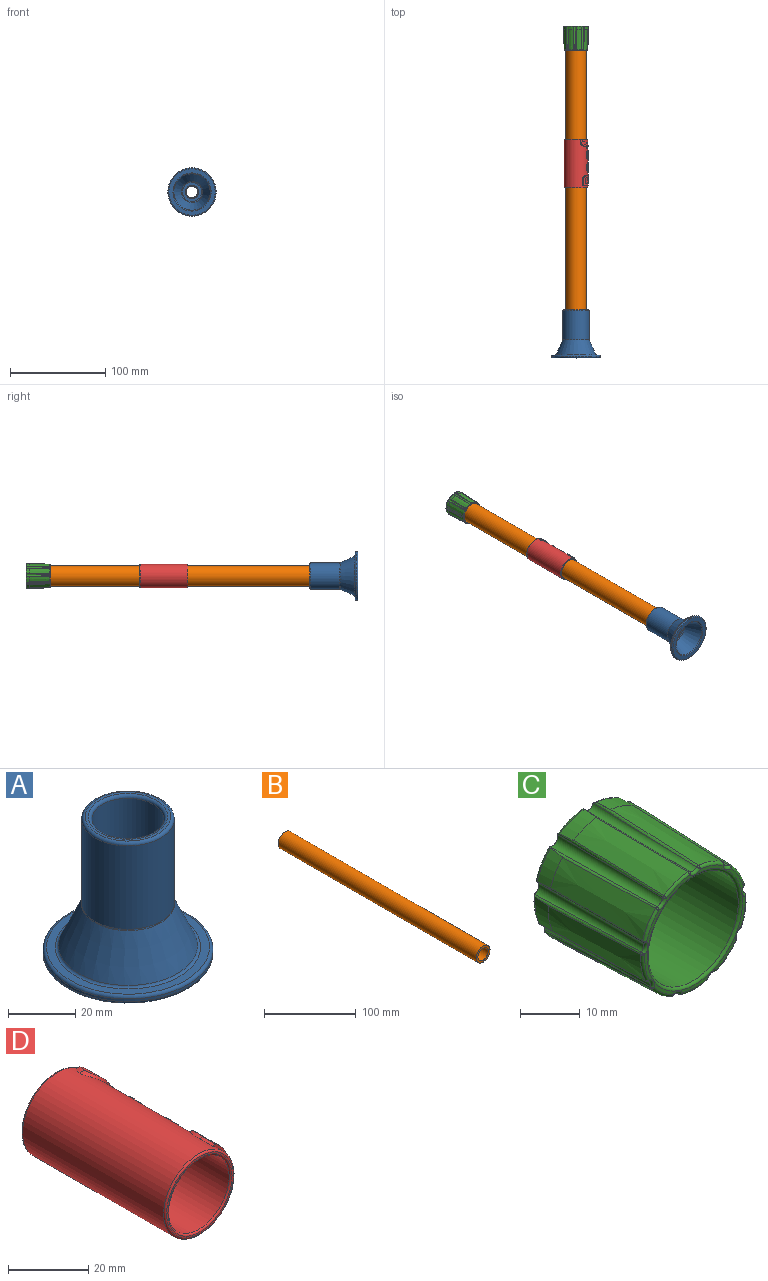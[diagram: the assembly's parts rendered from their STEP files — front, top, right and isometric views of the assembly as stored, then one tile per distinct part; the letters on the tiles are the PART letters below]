
ASSEMBLY  parts=4 mates=3
PART A: 22 faces, bbox 54.9x54.9x50.8 mm
  f0: cylinder r=6mm len=12.01mm, axis (0,0,-1), area 34.8mm2, adj f1,f21
  f1: torus R=7.05mm, axis (0,0,-1), area 66.1mm2, adj f0,f2
  f2: plane 20.23x20.23mm, normal (0,0,-1), area 165.2mm2, adj f1,f3
  f3: torus R=10.12mm, axis (0,0,-1), area 80.8mm2, adj f2,f4
  f4: cone r=19.05mm half-angle=24.1deg, axis (0,0,-1), area 1846.7mm2, adj f3,f5
  f5: torus R=20.01mm, axis (0,0,-1), area 147.6mm2, adj f4,f6
  f6: plane 48.66x48.66mm, normal (0,0,-1), area 602.3mm2, adj f5,f7
  f7: torus R=24.33mm, axis (0,0,-1), area 256.9mm2, adj f6,f8
  f8: cylinder r=25.37mm len=50.75mm, axis (0,0,-1), area 149.8mm2, adj f7,f9
  f9: torus R=24.33mm, axis (0,0,-1), area 256.9mm2, adj f8,f10
  f10: plane 48.66x48.66mm, normal (0,0,1), area 384.5mm2, adj f9,f11
  f11: torus R=21.67mm, axis (0,0,-1), area 159mm2, adj f10,f12
  f12: cone r=13.91mm half-angle=24.1deg, axis (0,0,-1), area 1812.8mm2, adj f11,f13
  f13: torus R=14.87mm, axis (0,0,-1), area 38.5mm2, adj f12,f14
  f14: cylinder r=13.82mm len=30.48mm, axis (0,0,-1), area 2645.9mm2, adj f13,f15
  f15: torus R=12.77mm, axis (0,0,-1), area 139.2mm2, adj f14,f16
  f16: plane 25.54x25.54mm, normal (0,0,1), area 71.4mm2, adj f15,f17
  f17: torus R=11.84mm, axis (0,0,-1), area 115.8mm2, adj f16,f18
  f18: cylinder r=10.79mm len=26.63mm, axis (0,0,-1), area 1806.1mm2, adj f17,f19
  f19: torus R=9.75mm, axis (0,0,-1), area 107.9mm2, adj f18,f20
  f20: plane 19.49x19.49mm, normal (0,0,1), area 142.1mm2, adj f19,f21
  f21: torus R=7.05mm, axis (0,0,-1), area 66.1mm2, adj f0,f20
PART B: 4 faces, bbox 21.3x304.8x21.3 mm
  f0: cylinder r=7.9mm len=304.8mm, axis (0,1,0), area 15128.3mm2, adj f2,f3
  f1: cylinder r=10.67mm len=304.8mm, axis (0,1,0), area 20430.4mm2, adj f2,f3
  f2: plane 21.34x21.34mm, normal (0,-1,0), area 161.5mm2, adj f0,f1
  f3: plane 21.34x21.34mm, normal (0,1,0), area 161.5mm2, adj f0,f1
PART C: 98 faces, bbox 28.5x32.6x28.4 mm
  f0: cylinder r=10.79mm len=21.59mm, axis (0,1,0), area 1271.4mm2, adj f31,f51
  f1: plane 23.87x23.81mm, normal (0,-1,0), area 37.5mm2, adj f41,f42,f43,f44,f45,f46,f47,f48
  f2: cylinder r=13.14mm len=5.84mm, axis (0,1,0), area 18.8mm2, adj f11,f38,f83,f97
  f3: cylinder r=13.14mm len=5.84mm, axis (0,1,0), area 18.8mm2, adj f12,f37,f87,f88
  f4: cylinder r=13.14mm len=5.38mm, axis (0,1,0), area 18.8mm2, adj f13,f36,f67,f92
  f5: cylinder r=13.14mm len=6.12mm, axis (0,1,0), area 18.8mm2, adj f14,f35,f63,f72
  f6: cylinder r=13.14mm len=4.76mm, axis (0,1,0), area 18.8mm2, adj f15,f34,f68,f77
  f7: cylinder r=13.14mm len=6.21mm, axis (0,1,0), area 18.8mm2, adj f16,f33,f73,f82
  f8: cylinder r=13.14mm len=4.76mm, axis (0,1,0), area 18.8mm2, adj f17,f50,f57,f78
  f9: cylinder r=13.14mm len=6.12mm, axis (0,1,0), area 18.8mm2, adj f18,f40,f53,f62
  f10: plane 25.27x25.22mm, normal (0,1,0), area 145.5mm2, adj f21,f22,f23,f24,f25,f26,f27,f28
  f11: cone r=12.43mm half-angle=1.9deg, axis (0,1,0), area 125.3mm2, adj f2,f45,f83,f97
  f12: cone r=12.43mm half-angle=1.9deg, axis (0,1,0), area 125.3mm2, adj f3,f46,f87,f88
  f13: cone r=12.43mm half-angle=1.9deg, axis (0,1,0), area 125.3mm2, adj f4,f47,f67,f92
  f14: cone r=12.43mm half-angle=1.9deg, axis (0,1,0), area 125.3mm2, adj f5,f48,f63,f72
  f15: cone r=12.43mm half-angle=1.9deg, axis (0,1,0), area 125.3mm2, adj f6,f49,f68,f77
  f16: cone r=12.43mm half-angle=1.9deg, axis (0,1,0), area 125.3mm2, adj f7,f41,f73,f82
  f17: cone r=12.43mm half-angle=1.9deg, axis (0,1,0), area 125.3mm2, adj f8,f42,f57,f78
  f18: cone r=12.43mm half-angle=1.9deg, axis (0,1,0), area 125.3mm2, adj f9,f43,f53,f62
  f19: cylinder r=13.14mm len=5.38mm, axis (0,1,0), area 18.8mm2, adj f20,f39,f58,f93
  f20: cone r=12.43mm half-angle=1.9deg, axis (0,1,0), area 125.3mm2, adj f19,f44,f58,f93
  f21: cylinder r=1.27mm len=24.89mm, axis (0,1,0), area 65.3mm2, adj f10,f38,f39,f93,f95,f97
  f22: cylinder r=1.27mm len=24.89mm, axis (0,1,0), area 65.3mm2, adj f10,f39,f40,f58,f60,f62
  f23: cylinder r=1.27mm len=24.89mm, axis (0,1,0), area 65.3mm2, adj f10,f40,f50,f53,f55,f57
  f24: cylinder r=1.27mm len=24.89mm, axis (0,1,0), area 65.3mm2, adj f10,f33,f50,f78,f80,f82
  f25: cylinder r=1.27mm len=24.89mm, axis (0,1,0), area 65.3mm2, adj f10,f33,f34,f73,f75,f77
  f26: cylinder r=1.27mm len=24.89mm, axis (0,1,0), area 65.3mm2, adj f10,f34,f35,f68,f70,f72
  f27: cylinder r=1.27mm len=24.89mm, axis (0,1,0), area 65.3mm2, adj f10,f35,f36,f63,f65,f67
  f28: cylinder r=1.27mm len=24.89mm, axis (0,1,0), area 65.3mm2, adj f10,f36,f37,f88,f90,f92
  f29: cylinder r=1.27mm len=24.89mm, axis (0,1,0), area 65.3mm2, adj f10,f37,f38,f83,f85,f87
  f30: cylinder r=7.94mm len=15.88mm, axis (0,1,0), area 154.5mm2, adj f32,f52
  f31: plane 21.59x21.59mm, normal (0,-1,0), area 142mm2, adj f0,f32
  f32: torus R=8.45mm, axis (0,1,0), area 40.7mm2, adj f30,f31
  f33: torus R=12.64mm, axis (0,-1,0), area 5.1mm2, adj f7,f10,f24,f25,f73,f82
  f34: torus R=12.64mm, axis (0,-1,0), area 5.1mm2, adj f6,f10,f25,f26,f68,f77
  f35: torus R=12.64mm, axis (0,-1,0), area 5.1mm2, adj f5,f10,f26,f27,f63,f72
  f36: torus R=12.64mm, axis (0,-1,0), area 5.1mm2, adj f4,f10,f27,f28,f67,f92
  f37: torus R=12.64mm, axis (0,-1,0), area 5.1mm2, adj f3,f10,f28,f29,f87,f88
  f38: torus R=12.64mm, axis (0,-1,0), area 5.1mm2, adj f2,f10,f21,f29,f83,f97
  f39: torus R=12.64mm, axis (0,-1,0), area 5.1mm2, adj f10,f19,f21,f22,f58,f93
  f40: torus R=12.64mm, axis (0,-1,0), area 5.1mm2, adj f9,f10,f22,f23,f53,f62
  f41: torus R=11.94mm, axis (0,-1,0), area 4.7mm2, adj f1,f16,f74,f81
  f42: torus R=11.94mm, axis (0,-1,0), area 4.7mm2, adj f1,f17,f56,f79
  f43: torus R=11.94mm, axis (0,-1,0), area 4.7mm2, adj f1,f18,f54,f61
  f44: torus R=11.94mm, axis (0,-1,0), area 4.7mm2, adj f1,f20,f59,f94
  f45: torus R=11.94mm, axis (0,-1,0), area 4.7mm2, adj f1,f11,f84,f96
  f46: torus R=11.94mm, axis (0,-1,0), area 4.7mm2, adj f1,f12,f86,f89
  f47: torus R=11.94mm, axis (0,-1,0), area 4.7mm2, adj f1,f13,f66,f91
  f48: torus R=11.94mm, axis (0,-1,0), area 4.7mm2, adj f1,f14,f64,f71
  f49: torus R=11.94mm, axis (0,-1,0), area 4.7mm2, adj f1,f15,f69,f76
  f50: torus R=12.64mm, axis (0,-1,0), area 5.1mm2, adj f8,f10,f23,f24,f57,f78
  f51: torus R=11.3mm, axis (0,-1,0), area 55mm2, adj f0,f1
  f52: torus R=10.48mm, axis (0,-1,0), area 222.1mm2, adj f10,f30
  f53: bspline ~32.55x1.47mm, area 13.9mm2, adj f9,f18,f23,f40,f54
  f54: sphere r=0.51mm, area 0.3mm2, adj f43,f53,f55
  f55: torus R=1.78mm, axis (0,-1,0), area 1.8mm2, adj f1,f23,f54,f56
  f56: sphere r=0.51mm, area 0.3mm2, adj f42,f55,f57
  f57: bspline ~32.59x1.44mm, area 13.9mm2, adj f8,f17,f23,f50,f56
  f58: bspline ~32.55x1.2mm, area 13.9mm2, adj f19,f20,f22,f39,f59
  f59: sphere r=0.51mm, area 0.3mm2, adj f44,f58,f60
  f60: torus R=1.78mm, axis (0,-1,0), area 1.8mm2, adj f1,f22,f59,f61
  f61: sphere r=0.51mm, area 0.3mm2, adj f43,f60,f62
  f62: bspline ~32.51x1.26mm, area 13.9mm2, adj f9,f18,f22,f40,f61
  f63: bspline ~32.51x1.26mm, area 13.9mm2, adj f5,f14,f27,f35,f64
  f64: sphere r=0.51mm, area 0.3mm2, adj f48,f63,f65
  f65: torus R=1.78mm, axis (0,-1,0), area 1.8mm2, adj f1,f27,f64,f66
  f66: sphere r=0.51mm, area 0.3mm2, adj f47,f65,f67
  f67: bspline ~32.56x1.2mm, area 13.9mm2, adj f4,f13,f27,f36,f66
  f68: bspline ~32.59x1.44mm, area 13.9mm2, adj f6,f15,f26,f34,f69
  f69: sphere r=0.51mm, area 0.3mm2, adj f49,f68,f70
  f70: torus R=1.78mm, axis (0,-1,0), area 1.8mm2, adj f1,f26,f69,f71
  f71: sphere r=0.51mm, area 0.3mm2, adj f48,f70,f72
  f72: bspline ~32.55x1.47mm, area 13.9mm2, adj f5,f14,f26,f35,f71
  f73: bspline ~32.52x1.39mm, area 13.9mm2, adj f7,f16,f25,f33,f74
  f74: sphere r=0.51mm, area 0.3mm2, adj f41,f73,f75
  f75: torus R=1.78mm, axis (0,-1,0), area 1.8mm2, adj f1,f25,f74,f76
  f76: sphere r=0.51mm, area 0.3mm2, adj f49,f75,f77
  f77: bspline ~32.58x1.34mm, area 13.9mm2, adj f6,f15,f25,f34,f76
  f78: bspline ~32.58x1.34mm, area 13.9mm2, adj f8,f17,f24,f50,f79
  f79: sphere r=0.51mm, area 0.3mm2, adj f42,f78,f80
  f80: torus R=1.78mm, axis (0,-1,0), area 1.8mm2, adj f1,f24,f79,f81
  f81: sphere r=0.51mm, area 0.3mm2, adj f41,f80,f82
  f82: bspline ~32.52x1.39mm, area 13.9mm2, adj f7,f16,f24,f33,f81
  f83: bspline ~32.53x1.16mm, area 13.9mm2, adj f2,f11,f29,f38,f84
  f84: sphere r=0.51mm, area 0.3mm2, adj f45,f83,f85
  f85: torus R=1.78mm, axis (0,-1,0), area 1.8mm2, adj f1,f29,f84,f86
  f86: sphere r=0.51mm, area 0.3mm2, adj f46,f85,f87
  f87: bspline ~32.53x1.16mm, area 13.9mm2, adj f3,f12,f29,f37,f86
  f88: bspline ~32.57x1.51mm, area 13.9mm2, adj f3,f12,f28,f37,f89
  f89: sphere r=0.51mm, area 0.3mm2, adj f46,f88,f90
  f90: torus R=1.78mm, axis (0,-1,0), area 1.8mm2, adj f1,f28,f89,f91
  f91: sphere r=0.51mm, area 0.3mm2, adj f47,f90,f92
  f92: bspline ~32.59x1.5mm, area 13.9mm2, adj f4,f13,f28,f36,f91
  f93: bspline ~32.58x1.5mm, area 13.9mm2, adj f19,f20,f21,f39,f94
  f94: sphere r=0.51mm, area 0.3mm2, adj f44,f93,f95
  f95: torus R=1.78mm, axis (0,-1,0), area 1.8mm2, adj f1,f21,f94,f96
  f96: sphere r=0.51mm, area 0.3mm2, adj f45,f95,f97
  f97: bspline ~32.57x1.51mm, area 13.9mm2, adj f2,f11,f21,f38,f96
PART D: 96 faces, bbox 26.7x50.8x26.7 mm
  f0: plane 0.8x0.11mm, normal (0,1,0), area 0.1mm2, adj f14,f20,f21,f62
  f1: plane 16.3x6.31mm, normal (0,-1,0), area 13.8mm2, adj f14,f24,f25,f62
  f2: plane 1.17x0.79mm, normal (0,1,0), area 0.9mm2, adj f14,f30,f31,f61
  f3: plane 1.65x1.46mm, normal (0,1,0), area 1.3mm2, adj f14,f34,f35,f61
  f4: plane 1.17x0.79mm, normal (0,1,0), area 0.9mm2, adj f14,f42,f43,f60
  f5: plane 1.65x1.46mm, normal (0,1,0), area 1.3mm2, adj f14,f46,f47,f60
  f6: plane 10.78x2.33mm, normal (0,1,0), area 8.4mm2, adj f14,f50,f58,f59
  f7: plane 10.78x2.33mm, normal (0,-1,0), area 8.4mm2, adj f14,f50,f51,f59
  f8: plane 1.2x0.84mm, normal (0,-1,0), area 0.7mm2, adj f9,f14,f51,f59
  f9: plane 2.2x1.23mm, normal (0,-0.29,0.96), area 2mm2, adj f8,f10,f14,f59
  f10: plane 1.3x0.68mm, normal (0,-1,0), area 0.6mm2, adj f9,f14,f52,f59
  f11: plane 3.54x1.53mm, normal (0,0.95,-0.31), area 2.1mm2, adj f14,f53,f54,f59
  f12: plane 1.37x0.79mm, normal (0,1,0), area 0.7mm2, adj f14,f56,f57,f59
  f13: plane 1.53x1.44mm, normal (0,1,0), area 1.2mm2, adj f14,f57,f58,f59
  f14: cylinder r=12.31mm len=49.78mm, axis (0,1,0), area 3445mm2, adj f0,f1,f2,f3,f4,f5,f6,f7
  f15: plane 23.6x23.6mm, normal (0,-1,0), area 35.9mm2, adj f94,f95
  f16: plane 23.6x23.6mm, normal (0,1,0), area 35.9mm2, adj f92,f93
  f17: extruded ~4.69x2.4mm, area 6mm2, adj f14,f18,f25,f62
  f18: extruded ~3.43x3.07mm, area 3.5mm2, adj f14,f17,f19,f62
  f19: extruded ~2.39x1.88mm, area 2.1mm2, adj f14,f18,f20,f62
  f20: extruded ~2.36x1.22mm, area 2.1mm2, adj f0,f14,f19,f62
  f21: extruded ~3.9x3.71mm, area 4.5mm2, adj f0,f14,f22,f62
  f22: extruded ~3.41x1.65mm, area 3mm2, adj f14,f21,f23,f62
  f23: extruded ~4.13x1.42mm, area 3.7mm2, adj f14,f22,f24,f62
  f24: plane 5.69x0.86mm, normal (0,0,-1), area 4.9mm2, adj f1,f14,f23,f62
  f25: plane 4.61x1.3mm, normal (0,0,1), area 6mm2, adj f1,f14,f17,f62
  f26: extruded ~4.58x1.64mm, area 3.8mm2, adj f14,f27,f37,f61
  f27: extruded ~4.7x1.68mm, area 3.9mm2, adj f14,f26,f28,f61
  f28: extruded ~3.91x1.74mm, area 3.8mm2, adj f14,f27,f29,f61
  f29: extruded ~3.63x1.61mm, area 3.5mm2, adj f14,f28,f30,f61
  f30: extruded ~3.99x1.75mm, area 3.4mm2, adj f2,f14,f29,f61
  f31: plane 8.42x0.76mm, normal (0,0,-1), area 6.4mm2, adj f2,f14,f32,f61
  f32: extruded ~3.27x1.26mm, area 2.7mm2, adj f14,f31,f33,f61
  f33: extruded ~2.9x1.18mm, area 2.6mm2, adj f14,f32,f34,f61
  f34: extruded ~3.9x1.09mm, area 3.2mm2, adj f3,f14,f33,f61
  f35: extruded ~1.86x1.16mm, area 1.7mm2, adj f3,f14,f36,f61
  f36: extruded ~2.11x0.97mm, area 1.8mm2, adj f14,f35,f37,f61
  f37: extruded ~4.28x1.65mm, area 4mm2, adj f14,f26,f36,f61
  f38: extruded ~4.58x1.64mm, area 3.8mm2, adj f14,f39,f49,f60
  f39: extruded ~4.7x1.68mm, area 3.9mm2, adj f14,f38,f40,f60
  f40: extruded ~3.91x1.74mm, area 3.8mm2, adj f14,f39,f41,f60
  f41: extruded ~3.63x1.61mm, area 3.5mm2, adj f14,f40,f42,f60
  f42: extruded ~3.99x1.75mm, area 3.4mm2, adj f4,f14,f41,f60
  f43: plane 8.42x0.76mm, normal (0,0,-1), area 6.4mm2, adj f4,f14,f44,f60
  f44: extruded ~3.27x1.26mm, area 2.7mm2, adj f14,f43,f45,f60
  f45: extruded ~2.9x1.18mm, area 2.6mm2, adj f14,f44,f46,f60
  f46: extruded ~3.9x1.09mm, area 3.2mm2, adj f5,f14,f45,f60
  f47: extruded ~1.86x1.16mm, area 1.7mm2, adj f5,f14,f48,f60
  f48: extruded ~2.11x0.97mm, area 1.8mm2, adj f14,f47,f49,f60
  f49: extruded ~4.28x1.65mm, area 4mm2, adj f14,f38,f48,f60
  f50: plane 1.85x0.86mm, normal (0,0,-1), area 1.6mm2, adj f6,f7,f14,f59
  f51: plane 2.18x0.82mm, normal (0,0,-1), area 1.8mm2, adj f7,f8,f14,f59
  f52: extruded ~6.57x4.51mm, area 9mm2, adj f10,f14,f53,f59
  f53: extruded ~2.44x2.28mm, area 3.9mm2, adj f11,f14,f52,f59
  f54: extruded ~1.83x1.61mm, area 2.2mm2, adj f11,f14,f55,f59
  f55: extruded ~1.97x1.55mm, area 2.1mm2, adj f14,f54,f56,f59
  f56: extruded ~2.89x2.24mm, area 2.3mm2, adj f12,f14,f55,f59
  f57: plane 3.11x0.87mm, normal (0,0,1), area 2.7mm2, adj f12,f13,f14,f59
  f58: plane 3.11x0.82mm, normal (0,0,-1), area 2.5mm2, adj f6,f13,f14,f59
  f59: cylinder r=13.06mm len=17.47mm, axis (0,1,0), area 52.5mm2, adj f6,f7,f8,f9,f10,f11,f12,f13
  f60: cylinder r=13.06mm len=12.67mm, axis (0,1,0), area 62.3mm2, adj f4,f5,f38,f39,f40,f41,f42,f43
  f61: cylinder r=13.06mm len=12.67mm, axis (0,1,0), area 62.3mm2, adj f2,f3,f26,f27,f28,f29,f30,f31
  f62: cylinder r=13.06mm len=16.3mm, axis (0,1,0), area 102.4mm2, adj f0,f1,f17,f18,f19,f20,f21,f22
  f63: cylinder r=12.31mm len=6.89mm, axis (0,1,0), area 39.2mm2, adj f64,f65,f66,f67,f68,f69,f70
  f64: plane 3.12x0.78mm, normal (0,0,1), area 2.4mm2, adj f62,f63,f65,f70
  f65: plane 5.34x3.88mm, normal (0,1,0), area 4.7mm2, adj f62,f63,f64,f66
  f66: plane 2.79x1.03mm, normal (0,0,-1), area 2.9mm2, adj f62,f63,f65,f67
  f67: extruded ~3.12x1.54mm, area 3.3mm2, adj f62,f63,f66,f68
  f68: extruded ~2.25x1.98mm, area 2.1mm2, adj f62,f63,f67,f69
  f69: extruded ~2.12x1.74mm, area 2mm2, adj f62,f63,f68,f70
  f70: extruded ~2.89x0.98mm, area 2.4mm2, adj f62,f63,f64,f69
  f71: cylinder r=12.31mm len=6.39mm, axis (0,1,0), area 19.2mm2, adj f72,f73,f74,f75,f76
  f72: extruded ~2.35x1.16mm, area 2.1mm2, adj f60,f71,f73,f76
  f73: extruded ~2.23x1.15mm, area 2mm2, adj f60,f71,f72,f74
  f74: extruded ~2.68x1.34mm, area 2.2mm2, adj f60,f71,f73,f75
  f75: plane 6.39x0.76mm, normal (0,0,1), area 4.9mm2, adj f60,f71,f74,f76
  f76: extruded ~2.65x1.34mm, area 2.2mm2, adj f60,f71,f72,f75
  f77: cylinder r=12.31mm len=6.39mm, axis (0,1,0), area 19.2mm2, adj f78,f79,f80,f81,f82
  f78: extruded ~2.35x1.16mm, area 2.1mm2, adj f61,f77,f79,f82
  f79: extruded ~2.23x1.15mm, area 2mm2, adj f61,f77,f78,f80
  f80: extruded ~2.68x1.34mm, area 2.2mm2, adj f61,f77,f79,f81
  f81: plane 6.39x0.76mm, normal (0,0,1), area 4.9mm2, adj f61,f77,f80,f82
  f82: extruded ~2.65x1.34mm, area 2.2mm2, adj f61,f77,f78,f81
  f83: cylinder r=12.31mm len=7.37mm, axis (0,1,0), area 41.6mm2, adj f84,f85,f86,f87,f88,f89,f90
  f84: plane 6.1x1.57mm, normal (0,1,0), area 4.7mm2, adj f62,f83,f85,f90
  f85: plane 3.25x0.76mm, normal (0,0,-1), area 2.5mm2, adj f62,f83,f84,f86
  f86: extruded ~3.1x0.84mm, area 2.5mm2, adj f62,f83,f85,f87
  f87: extruded ~2.23x1.02mm, area 1.9mm2, adj f62,f83,f86,f88
  f88: extruded ~2.39x1.25mm, area 2.1mm2, adj f62,f83,f87,f89
  f89: extruded ~2.97x1.05mm, area 2.5mm2, adj f62,f83,f88,f90
  f90: plane 3.4x0.81mm, normal (0,0,1), area 2.7mm2, adj f62,f83,f84,f89
  f91: cylinder r=10.79mm len=49.78mm, axis (0,1,0), area 3376.7mm2, adj f92,f94
  f92: torus R=11.3mm, axis (0,-1,0), area 55mm2, adj f16,f91
  f93: torus R=11.8mm, axis (0,-1,0), area 60.8mm2, adj f14,f16
  f94: torus R=11.3mm, axis (0,-1,0), area 55mm2, adj f15,f91
  f95: torus R=11.8mm, axis (0,-1,0), area 60.8mm2, adj f14,f15
PLACE A rot(axis=(-1,0,0),90deg) t=(79.12,-332.97,5.51)mm
PLACE B rot(axis=(0,-1,0),0.1deg) t=(79.12,5.38,5.51)mm
PLACE C rot(axis=(0,-1,0),5.3deg) t=(79.12,15.45,5.51)mm
PLACE D rot(axis=(0,-1,0),1.5deg) t=(79.12,-103.68,5.51)mm
MATE cylindrical B.f1 <-> C.f0  axis (0,1,0) through (79.12,5.38,5.51)mm
MATE cylindrical A.f0 <-> B.f1  axis (0,-1,0) through (79.12,-283.22,5.51)mm
MATE cylindrical D.f91 <-> B.f1  axis (0,1,0) through (79.12,-153.97,5.51)mm
